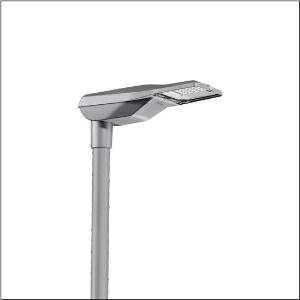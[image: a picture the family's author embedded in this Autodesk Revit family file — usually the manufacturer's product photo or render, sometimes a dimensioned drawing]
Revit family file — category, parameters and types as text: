
# Revit family: streetlight_sl_21_iq_micro___st0_8a_5xe1c31g08db_5951
name_source: partatom
category: Lighting Fixtures
units: mm (PartAtom-declared; Revit-internal decimal feet)

## family parameters
Cut with Voids When Loaded = No
Host = Face
Light Source = No
Part Type = Normal
Room Calculation Point = No
Round Connector Dimension = Use Diameter
Shared = No

## types (1)
- --- (1 x LED, 4810 lm, 36.4 W, 3000K)
    Apparent Load = 36 VA
    CIE Flux Codes = 38 75 97 100 100
    Color Rendering = 70
    Color Temperature = 3000K
    Default Elevation = 1800 mm
    Description = Streetlight SL 21 iQ micro, mast luminaire, primary light control with lens, of PMMA, primary optical cover: cover, of toughened safety glass, transparent, light distribution: ST0.8a, light emission: direct distribution, primary light characteristic: asymmetric, installation type: post-top, side-entry, LED, High Power LED, rated luminous flux: 4.810lm, luminous efficacy: 132lm/W, light colour: 730, colour temperature: 3000K, control: Street-Remote, Auto-Match, Temp-Guard, Lumen-Switch, Night-Set, Smart-Wire, Light-Fading, Desk-Remote (wireless, voltage-free reading and setting of iQ features in the workshop via application-optimized NFC function/RFID function), optimised constant luminous flux control (CLO 2.0), presetting dimming linear, mains connection: 220..240V, AC, 50/60Hz, start of lifetime: 36W, end of service life: 38W, reduction: 16W, luminaire housing, of diecast aluminium, powder-coated, Siteco® metallic grey (DB 702S), corrosivity category C5 mid according to DIN EN ISO 12944, please order mast flange separately, inclination adjustable: 0°, 5°, 10°, 15°, sealing non-destructively replaceable, multi-level sealing system, length: 528mm, width: 235mm, height: 110mm, mast flange for spigot size: 42mm (side-entry): 5XC10008XM4, 60/48mm (side-entry/post-top): 5XC10108XM2, 76/60mm (side-entry/post-top): 5XC10108XM1, protection rating (complete): IP66, insulation class (complete): insulation class II (safety insulation), certification: CE, ENEC, ENEC+, VDE, impact resistance: IK09, permissible operating ambient temperature for outdoor applications: -40..+50°C, standard-compliant lighting for roads and squares, packaging unit: 1 piece

Light Distribution: ST0.8a
    Height = 110 mm
    Lamp = 1 x LED
    Lamp Light Flux = 4810 lm
    Lamp Power = 36.4 W
    Lamp count = 1
    Length = 528 mm
    Luminous efficacy = 132 lm/W
    Manufacturer = Siteco
    ModVariant = No
    Model = 5XE1C31G08DB
    Number of Poles = 1
    OnlyDefault = Yes
    Power Factor = 1
    Product Name = Streetlight SL 21 iQ micro | ST0.8a
    Product group = mast luminaire | pylon top
    ProductGroupID = 6100
    Protection Class = Protection class II
    Protection Degree = IP 66
    RLX_Detail_Level = 1
    RLX_Emergency_Light_Flux = 0 lm
    RLX_Emergency_Type = 0
    RLX_Emergency_Type_DB = No
    RlxData = <blob elided: 98997 chars, md5=fb0b9569>
    Socket = socket
    Standby Power = 0 W
    System Light Flux = 4810 lm
    System Power = 36 W
    Type Comments = factory setting: luminous flux: 100 % | dim-lin: 254 | 715 mA
    Type Image = l_1006881.jpg
    URL = http://relux.com
    VarID = @adj_086845
    Voltage = 0 V
    Weight = 0.00 kg
    Width = 235 mm

## geometry (parser evidence)
native form markers: Blend x4, Sweep x10
no freeform markers — native parametric forms only
